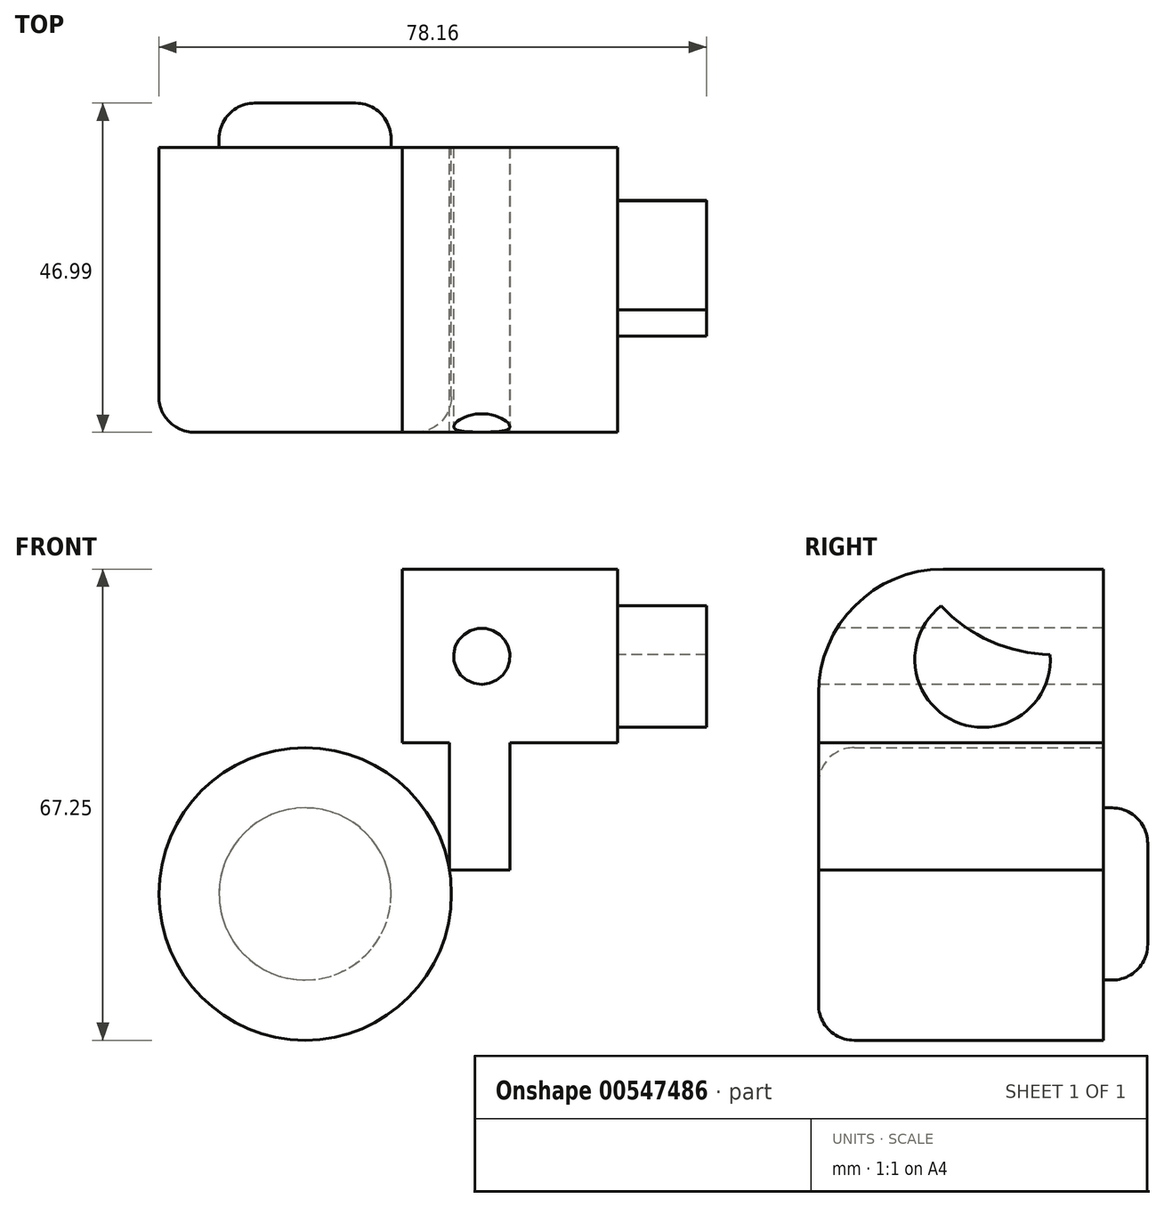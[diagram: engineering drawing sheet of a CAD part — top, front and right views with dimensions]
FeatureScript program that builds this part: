
annotation { "Feature Type Name" : "Feature", "Feature Type Description" : "" }
export const myFeature = defineFeature(function(context is Context, id is Id, definition is map)
    precondition{}
    {
        {
            var Q0;
            Q0=qCreatedBy(makeId("Front.planeOp"),FACE);
            var sketch = newSketch(context, id + "F0", { "sketchPlane" : qUnion([Q0])});
            skCircle(sketch, "E0", {"center": v(0, 0) * mm, "radius": 20.88 * mm});
            skLineSegment(sketch, "E1.bottom", {"start": v(13.88, 21.55) * mm, "end": v(44.58, 21.55) * mm});
            skLineSegment(sketch, "E1.top", {"start": v(13.88, 46.37) * mm, "end": v(44.58, 46.37) * mm});
            skLineSegment(sketch, "E1.left", {"start": v(13.88, 21.55) * mm, "end": v(13.88, 46.37) * mm});
            skLineSegment(sketch, "E1.right", {"start": v(44.58, 21.55) * mm, "end": v(44.58, 46.37) * mm});
            skLineSegment(sketch, "E2.bottom", {"start": v(29.23, 21.55) * mm, "end": v(20.6, 21.55) * mm});
            skLineSegment(sketch, "E2.top", {"start": v(29.23, 3.44) * mm, "end": v(20.6, 3.44) * mm});
            skLineSegment(sketch, "E2.left", {"start": v(29.23, 21.55) * mm, "end": v(29.23, 3.44) * mm});
            skLineSegment(sketch, "E2.right", {"start": v(20.6, 21.55) * mm, "end": v(20.6, 3.44) * mm});
            skSolve(sketch);
        }
        {
            var Q0;
            Q0 = qSketchRegion(id + "F0", true);
            extrude(context, id + "F1", {"entities" : qUnion([Q0]), "depth" : 40.64 * mm, "offsetDistance" : 25.4 * mm});
        }
        {
            var Q0;
            Q0=makeQuery(id+"F1.opExtrude","CAP_EDGE",EDGE,{"disambiguationData":[OSD([sQuery(id+"F0.wireOp",EDGE,"E0")])],"isStart":false});
            fillet(context, id + "F2", {"entities" : qUnion([Q0]), "radius" : 5.08 * mm, "tangentPropagation" : true, "allowEdgeOverflow" : false});
        }
        {
            var Q0;
            Q0=makeQuery(id+"F1.opExtrude","CAP_FACE",FACE,{"disambiguationData":[OSD([sQuery(id+"F0.wireOp",EDGE,"E0")])],"isStart":true});
            var sketch = newSketch(context, id + "F3", { "sketchPlane" : qUnion([Q0])});
            skCircle(sketch, "E3", {"center": v(0, 0) * mm, "radius": 12.28 * mm});
            skSolve(sketch);
        }
        {
            var Q0;
            Q0=makeQuery(id+"F3.imprint","IMPRINT",FACE,{"disambiguationData":[TD([[makeQuery(id+"F3.imprint","IMPRINT",EDGE,{"derivedFrom":sQuery(id+"F3.wireOp",EDGE,"E3")}),1.0]])]});
            var Q1;
            Q1=sQuery(id+"F3.wireOp",EDGE,"E3");
            extrude(context, id + "F4", {"entities" : qUnion([Q0]), "operationType" : NewBodyOperationType.ADD, "surfaceEntities" : qUnion([Q1]), "endBound" : BoundingType.SYMMETRIC, "depth" : 12.7 * mm, "offsetDistance" : 25.4 * mm});
        }
        {
            var Q0;
            Q0=makeQuery(id+"F4.opExtrude","CAP_EDGE",EDGE,{"disambiguationData":[OSD([sQuery(id+"F3.wireOp",EDGE,"E3")])],"isStart":false});
            fillet(context, id + "F5", {"entities" : qUnion([Q0]), "radius" : 5.08 * mm, "tangentPropagation" : true, "allowEdgeOverflow" : false});
        }
        {
            var Q0;
            Q0=makeQuery(id+"F1.opExtrude","CAP_EDGE",EDGE,{"disambiguationData":[OSD([sQuery(id+"F0.wireOp",EDGE,"E1.top")])],"isStart":false});
            fillet(context, id + "F6", {"entities" : qUnion([Q0]), "radius" : 17.78 * mm, "tangentPropagation" : true, "allowEdgeOverflow" : false});
        }
        {
            var Q0;
            Q0=makeQuery(id+"F1.opExtrude","SWEPT_FACE",FACE,{"disambiguationData":[OSD([sQuery(id+"F0.wireOp",EDGE,"E1.right")])]});
            var sketch = newSketch(context, id + "F7", { "sketchPlane" : qUnion([Q0])});
            skArc(sketch, "E4", {"start": v(-23.13, 41.1) * mm, "mid": v(-21.16, 24.62) * mm, "end": v(-7.57, 34.17) * mm});
            skArc(sketch, "E5", {"start": v(-23.13, 41.1) * mm, "mid": v(-16.06, 36.06) * mm, "end": v(-7.57, 34.17) * mm});
            skSolve(sketch);
        }
        {
            var Q0;
            Q0=makeQuery(id+"F7.imprint","IMPRINT",FACE,{"disambiguationData":[TD([[makeQuery(id+"F7.imprint","IMPRINT",EDGE,{"derivedFrom":sQuery(id+"F7.wireOp",EDGE,"E4")}),1.0]])]});
            extrude(context, id + "F8", {"entities" : qUnion([Q0]), "operationType" : NewBodyOperationType.ADD, "depth" : 12.7 * mm, "offsetDistance" : 25.4 * mm});
        }
        {
            var Q0;
            Q0=makeQuery(id+"F1.opExtrude","CAP_FACE",FACE,{"disambiguationData":[OSD([sQuery(id+"F0.wireOp",EDGE,"E1.bottom"),sQuery(id+"F0.wireOp",EDGE,"E1.top"),sQuery(id+"F0.wireOp",EDGE,"E1.left"),sQuery(id+"F0.wireOp",EDGE,"E1.right"),sQuery(id+"F0.wireOp",EDGE,"E2.top"),sQuery(id+"F0.wireOp",EDGE,"E2.left"),sQuery(id+"F0.wireOp",EDGE,"E2.right")])],"isStart":false});
            var sketch = newSketch(context, id + "F9", { "sketchPlane" : qUnion([Q0])});
            skCircle(sketch, "E6", {"center": v(25.21, 33.93) * mm, "radius": 4.01 * mm});
            skSolve(sketch);
        }
        {
            var Q0;
            Q0=makeQuery(id+"F9.imprint","IMPRINT",FACE,{"disambiguationData":[TD([[makeQuery(id+"F9.imprint","IMPRINT",EDGE,{"derivedFrom":sQuery(id+"F9.wireOp",EDGE,"E6")}),1.0]])]});
            extrude(context, id + "F10", {"entities" : qUnion([Q0]), "operationType" : NewBodyOperationType.REMOVE, "endBound" : BoundingType.THROUGH_ALL, "oppositeDirection" : true, "depth" : 33.02 * mm, "offsetDistance" : 25.4 * mm});
        }
    });
